# Revit family: BuroSeating_Konfurb Orbit HB_Sled
name_source: partatom
category: Furniture
units: mm (PartAtom-declared; Revit-internal decimal feet)

## family parameters
Always vertical = Yes
Cut with Voids When Loaded = No
OmniClass Number = 23.40.70.14.64.11
OmniClass Title = Office Furniture
Room Calculation Point = No
Shared = No
Work Plane-Based = No

## types (1)
- Konfurb Orbit Sled Base High Back
    Assembly Code = E2020
    BaseOffset = 18 mm  [stored 0.0590551 ft]
    Default Elevation = 0 mm  [stored 0 ft]
    Description = Konfurb Orbit Sled Base High Back
    FeetMaterial = BuroSeating_Plastic_Black
    FrameMaterial = BuroSeating_Metal_Chrome_Semi-Polished
    Manufacturer = Buro Seating
    Model = KON182
    NominalArmHeight = 625mm
    NominalDepth = 655 mm  [stored 2.14895 ft]
    NominalHeight = 1265 mm  [stored 4.15026 ft]
    NominalWidth = 650 mm  [stored 2.13255 ft]
    ProductGroup = Konfurb Orbit
    ProductPageURL AU = https://buroseating.com
    ProductPageURL NZ = https://buroseating.co.nz
    ProductRange = Konfurb
    SeatBackHeght = 805 mm  [stored 2.64108 ft]
    SeatDepth = 470 mm  [stored 1.54199 ft]
    SeatHeight = 460 mm  [stored 1.50919 ft]
    SeatWidth = 515 mm  [stored 1.68963 ft]
    URL = https://buroseating.co.nz
    URL AU = https://buroseating.com
    WarrantyDescription = Full 5 year guarantee (excluding upholstery)

note: [stored X ft] marks values corroborated as IEEE doubles in the binary element streams (Revit-internal decimal feet)

## geometry (parser evidence)
native form markers: Sweep x5
no freeform markers — native parametric forms only
